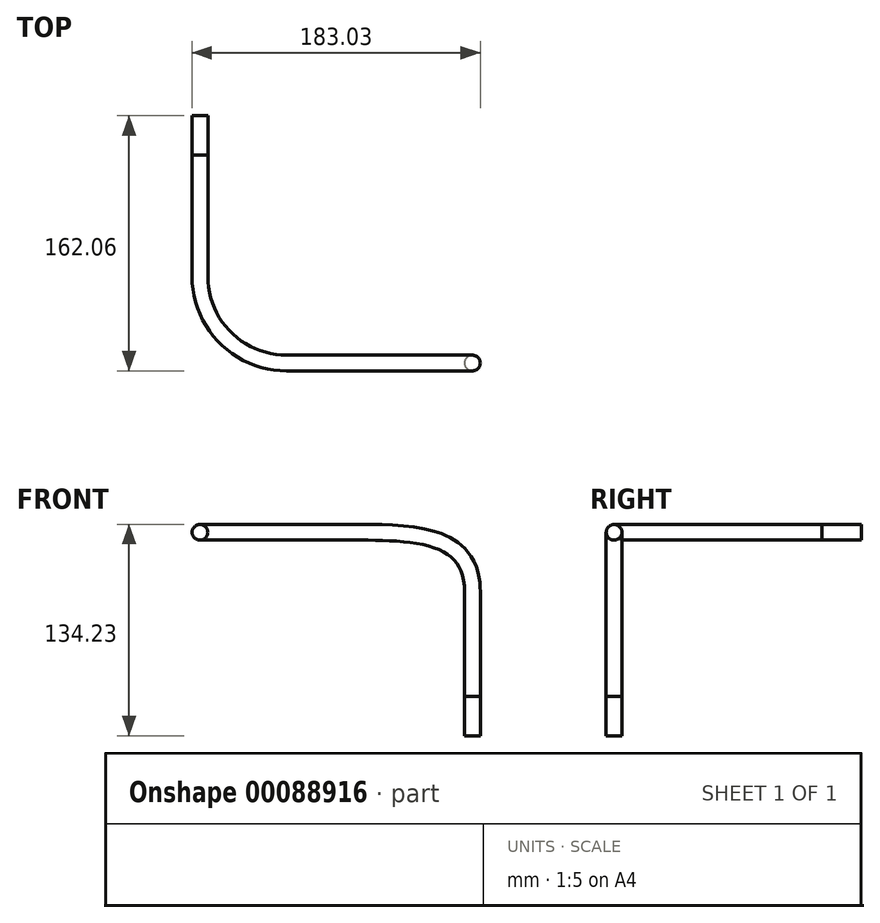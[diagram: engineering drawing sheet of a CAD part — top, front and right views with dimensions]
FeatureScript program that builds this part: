
annotation { "Feature Type Name" : "Feature", "Feature Type Description" : "" }
export const myFeature = defineFeature(function(context is Context, id is Id, definition is map)
    precondition{}
    {
        {
            var Q0;
            Q0=qCreatedBy(makeId("Top.planeOp"),FACE);
            var sketch = newSketch(context, id + "F0", { "sketchPlane" : qUnion([Q0])});
            skCircle(sketch, "E0", {"center": v(105.1, -132.06) * mm, "radius": 5 * mm});
            skSolve(sketch);
        }
        {
            var Q0;
            Q0=qCreatedBy(makeId("Front.planeOp"),FACE);
            var sketch = newSketch(context, id + "F1", { "sketchPlane" : qUnion([Q0])});
            skCircle(sketch, "E1", {"center": v(-67.93, 104.23) * mm, "radius": 5 * mm});
            skSolve(sketch);
        }
        {
            var Q0;
            Q0=makeQuery(id+"F0.imprint","IMPRINT",FACE,{"disambiguationData":[TD([[makeQuery(id+"F0.imprint","IMPRINT",EDGE,{"derivedFrom":sQuery(id+"F0.wireOp",EDGE,"E0")}),1.0]])]});
            extrude(context, id + "F2", {"entities" : qUnion([Q0]), "oppositeDirection" : true, "depth" : 25 * mm});
        }
        {
            var Q0;
            Q0=makeQuery(id+"F1.imprint","IMPRINT",FACE,{"disambiguationData":[TD([[makeQuery(id+"F1.imprint","IMPRINT",EDGE,{"derivedFrom":sQuery(id+"F1.wireOp",EDGE,"E1")}),1.0]])]});
            extrude(context, id + "F3", {"entities" : qUnion([Q0]), "oppositeDirection" : true, "depth" : 25 * mm});
        }
        {
            var Q0;
            Q0=qCreatedBy(makeId("Front.planeOp"),FACE);
            var Q1;
            Q1=sQuery(id+"F0.wireOp",VERTEX,"E0.center");
            cPlane(context, id + "F4", {"entities" : qUnion([Q0, Q1]), "cplaneType" : CPlaneType.PLANE_POINT, "offset" : 150 * mm, "width" : 150 * mm, "height" : 150 * mm});
        }
        {
            var Q0;
            Q0=sQuery(id+"F1.wireOp",VERTEX,"E1.center");
            var Q1;
            Q1=qCreatedBy(makeId("Top.planeOp"),FACE);
            cPlane(context, id + "F5", {"entities" : qUnion([Q0, Q1]), "cplaneType" : CPlaneType.PLANE_POINT, "offset" : 150 * mm, "width" : 150 * mm, "height" : 150 * mm});
        }
        {
            var Q0;
            Q0=qCreatedBy(id+"F5.planeOp",FACE);
            var sketch = newSketch(context, id + "F6", { "sketchPlane" : qUnion([Q0])});
            skLineSegment(sketch, "E2", {"start": v(-67.93, 0) * mm, "end": v(-67.93, -77.06) * mm});
            skLineSegment(sketch, "E3", {"start": v(-12.93, -132.06) * mm, "end": v(34.3, -132.06) * mm});
            skPoint(sketch, "E4.visualSharp", {"position": v(-67.93, -132.06) * mm});
            skArc(sketch, "E4.filletArc", {"start": v(-67.93, -77.06) * mm, "mid": v(-51.82, -115.95) * mm, "end": v(-12.93, -132.06) * mm});
            skSolve(sketch);
        }
        {
            var Q0;
            Q0=qCreatedBy(id+"F4.planeOp",FACE);
            var sketch = newSketch(context, id + "F7", { "sketchPlane" : qUnion([Q0])});
            skLineSegment(sketch, "E5", {"start": v(105.1, 0) * mm, "end": v(105.1, 66.39) * mm});
            skLineSegment(sketch, "E6.0", {"start": v(-12.93, 104.23) * mm, "end": v(34.3, 104.23) * mm, "construction": true});
            skFitSpline(sketch, "E7", {"points": [v(34.3, 104.23) * mm, v(105.1, 66.39) * mm], "startDerivative": vector(120.97, 0) * mm, "endDerivative": vector(0, -103.24) * mm});
            skSolve(sketch);
        }
        {
            var Q0;
            Q0=makeQuery(id+"F1.imprint","IMPRINT",FACE,{"disambiguationData":[TD([[makeQuery(id+"F1.imprint","IMPRINT",EDGE,{"derivedFrom":sQuery(id+"F1.wireOp",EDGE,"E1")}),1.0]])]});
            var Q1;
            Q1=sQuery(id+"F6.wireOp",EDGE,"E2");
            var Q2;
            Q2=sQuery(id+"F6.wireOp",EDGE,"E4.filletArc");
            var Q3;
            Q3=sQuery(id+"F6.wireOp",EDGE,"E3");
            var Q4;
            Q4=sQuery(id+"F7.wireOp",EDGE,"E7");
            var Q5;
            Q5=sQuery(id+"F7.wireOp",EDGE,"E5");
            sweep(context, id + "F8", {"profiles" : qUnion([Q0]), "path" : qUnion([Q1, Q2, Q3, Q4, Q5])});
        }
    });
